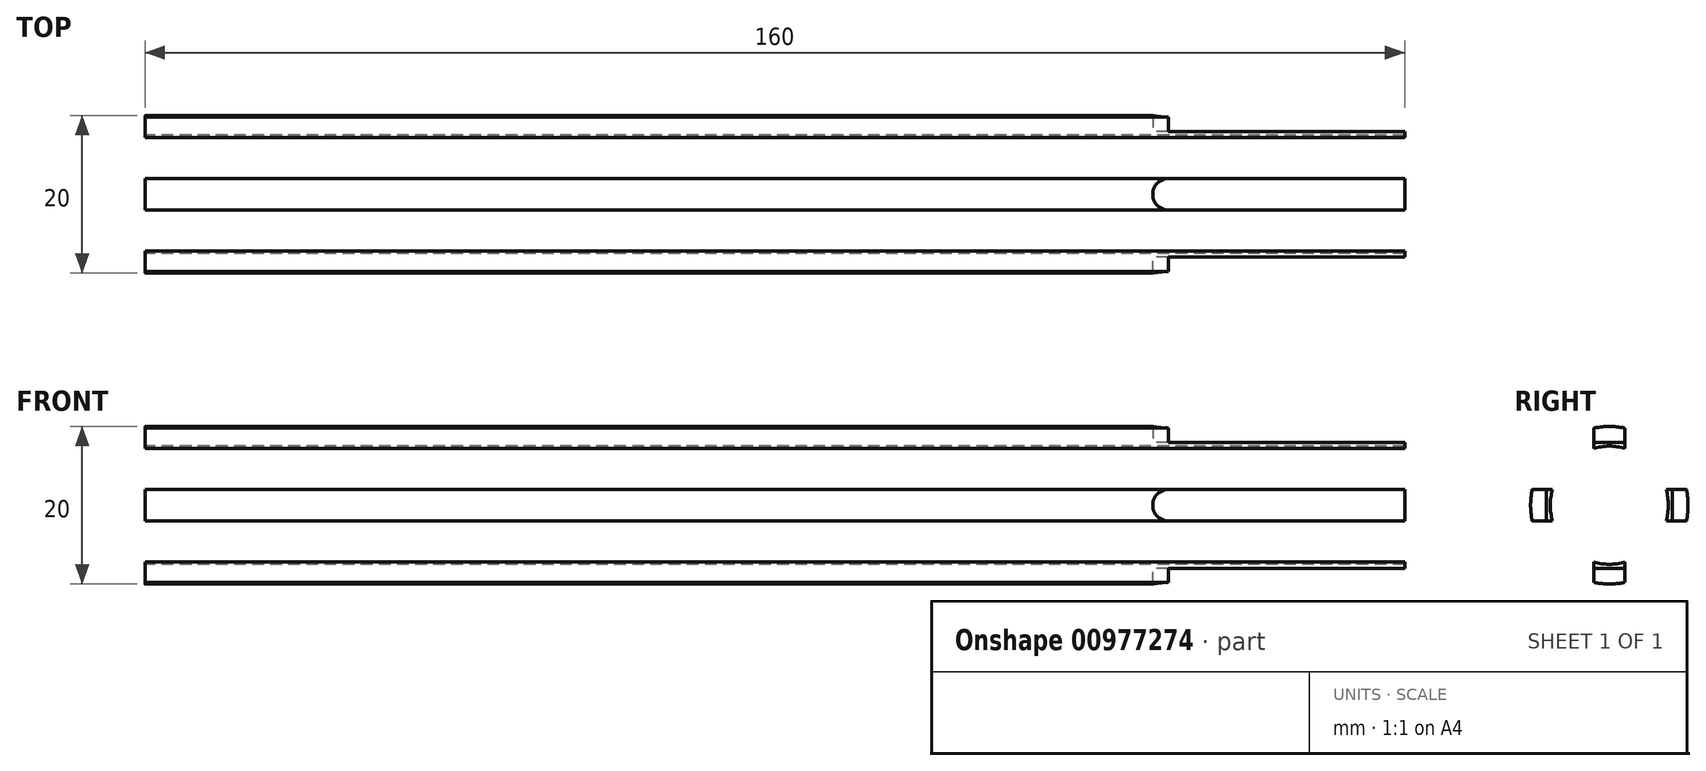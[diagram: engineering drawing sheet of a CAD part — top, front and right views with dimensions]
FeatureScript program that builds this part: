
annotation { "Feature Type Name" : "Feature", "Feature Type Description" : "" }
export const myFeature = defineFeature(function(context is Context, id is Id, definition is map)
    precondition{}
    {
        {
            var Q0;
            Q0=qCreatedBy(makeId("Right.planeOp"),FACE);
            var sketch = newSketch(context, id + "F0", { "sketchPlane" : qUnion([Q0])});
            skCircle(sketch, "E0", {"center": v(0, 0) * mm, "radius": 7.5 * mm});
            skCircle(sketch, "E1", {"center": v(0, 0) * mm, "radius": 10 * mm});
            skLineSegment(sketch, "E2.bottom", {"start": v(-2, 12.5) * mm, "end": v(2, 12.5) * mm});
            skLineSegment(sketch, "E2.top", {"start": v(-2, -12.5) * mm, "end": v(2, -12.5) * mm});
            skLineSegment(sketch, "E2.left", {"start": v(-2, 12.5) * mm, "end": v(-2, -12.5) * mm});
            skLineSegment(sketch, "E2.right", {"start": v(2, 12.5) * mm, "end": v(2, -12.5) * mm});
            skLineSegment(sketch, "E3.bottom", {"start": v(12.5, -2) * mm, "end": v(-12.5, -2) * mm});
            skLineSegment(sketch, "E3.top", {"start": v(12.5, 2) * mm, "end": v(-12.5, 2) * mm});
            skLineSegment(sketch, "E3.left", {"start": v(12.5, -2) * mm, "end": v(12.5, 2) * mm});
            skLineSegment(sketch, "E3.right", {"start": v(-12.5, -2) * mm, "end": v(-12.5, 2) * mm});
            skLineSegment(sketch, "E4.bottom", {"start": v(-2, 8) * mm, "end": v(2, 8) * mm});
            skLineSegment(sketch, "E4.top", {"start": v(-2, -8) * mm, "end": v(2, -8) * mm});
            skLineSegment(sketch, "E4.left", {"start": v(-2, 8) * mm, "end": v(-2, -8) * mm});
            skLineSegment(sketch, "E4.right", {"start": v(2, 8) * mm, "end": v(2, -8) * mm});
            skLineSegment(sketch, "E5.bottom", {"start": v(8, 2) * mm, "end": v(-8, 2) * mm});
            skLineSegment(sketch, "E5.top", {"start": v(8, -2) * mm, "end": v(-8, -2) * mm});
            skLineSegment(sketch, "E5.left", {"start": v(8, 2) * mm, "end": v(8, -2) * mm});
            skLineSegment(sketch, "E5.right", {"start": v(-8, 2) * mm, "end": v(-8, -2) * mm});
            skSolve(sketch);
        }
        {
            var Q0;
            {var subQ5=sQuery(id+"F0.wireOp",EDGE,"E4.right");var subQ9=sQuery(id+"F0.wireOp",EDGE,"E0");var subQ10=makeQuery(id+"F0.imprint","INTERSECT",VERTEX,{"disambiguationData":[OD(0.0)],"derivedFrom":[subQ9,subQ5]});Q0=makeQuery(id+"F0.imprint","IMPRINT",FACE,{"disambiguationData":[TD([[makeQuery(id+"F0.imprint","IMPRINT",EDGE,{"disambiguationData":[TD([[subQ10,1.0]])],"derivedFrom":subQ9}),-1.0]])]});}
            var Q1;
            {var subQ0=sQuery(id+"F0.wireOp",EDGE,"E4.left");var subQ8=sQuery(id+"F0.wireOp",EDGE,"E0");var subQ11=makeQuery(id+"F0.imprint","INTERSECT",VERTEX,{"disambiguationData":[OD(0.0)],"derivedFrom":[subQ8,subQ0]});Q1=makeQuery(id+"F0.imprint","IMPRINT",FACE,{"disambiguationData":[TD([[makeQuery(id+"F0.imprint","IMPRINT",EDGE,{"disambiguationData":[TD([[subQ11,-1.0]])],"derivedFrom":subQ8}),-1.0]])]});}
            var Q2;
            {var subQ0=sQuery(id+"F0.wireOp",EDGE,"E4.right");var subQ1=sQuery(id+"F0.wireOp",EDGE,"E0");var subQ2=makeQuery(id+"F0.imprint","INTERSECT",VERTEX,{"disambiguationData":[OD(0.0)],"derivedFrom":[subQ1,subQ0]});Q2=makeQuery(id+"F0.imprint","IMPRINT",FACE,{"disambiguationData":[TD([[makeQuery(id+"F0.imprint","IMPRINT",EDGE,{"disambiguationData":[TD([[subQ2,1.0]])],"derivedFrom":subQ1}),1.0]])]});}
            var Q3;
            {var subQ0=sQuery(id+"F0.wireOp",EDGE,"E4.right");var subQ1=sQuery(id+"F0.wireOp",EDGE,"E0");var subQ2=makeQuery(id+"F0.imprint","INTERSECT",VERTEX,{"disambiguationData":[OD(0.0)],"derivedFrom":[subQ1,subQ0]});Q3=makeQuery(id+"F0.imprint","IMPRINT",FACE,{"disambiguationData":[TD([[makeQuery(id+"F0.imprint","IMPRINT",EDGE,{"disambiguationData":[TD([[subQ2,-1.0]])],"derivedFrom":subQ1}),1.0]])]});}
            var Q4;
            {var subQ0=sQuery(id+"F0.wireOp",EDGE,"E4.left");var subQ1=sQuery(id+"F0.wireOp",EDGE,"E0");var subQ2=makeQuery(id+"F0.imprint","INTERSECT",VERTEX,{"disambiguationData":[OD(0.0)],"derivedFrom":[subQ1,subQ0]});Q4=makeQuery(id+"F0.imprint","IMPRINT",FACE,{"disambiguationData":[TD([[makeQuery(id+"F0.imprint","IMPRINT",EDGE,{"disambiguationData":[TD([[subQ2,-1.0]])],"derivedFrom":subQ1}),1.0]])]});}
            var Q5;
            {var subQ0=sQuery(id+"F0.wireOp",EDGE,"E5.bottom");var subQ1=sQuery(id+"F0.wireOp",EDGE,"E0");var subQ2=makeQuery(id+"F0.imprint","INTERSECT",VERTEX,{"disambiguationData":[OD(1.0)],"derivedFrom":[subQ1,subQ0]});Q5=makeQuery(id+"F0.imprint","IMPRINT",FACE,{"disambiguationData":[TD([[makeQuery(id+"F0.imprint","IMPRINT",EDGE,{"disambiguationData":[TD([[subQ2,-1.0]])],"derivedFrom":subQ1}),1.0]])]});}
            var Q6;
            {var subQ0=sQuery(id+"F0.wireOp",EDGE,"E5.bottom");var subQ1=sQuery(id+"F0.wireOp",EDGE,"E0");var subQ2=makeQuery(id+"F0.imprint","INTERSECT",VERTEX,{"disambiguationData":[OD(0.0)],"derivedFrom":[subQ1,subQ0]});Q6=makeQuery(id+"F0.imprint","IMPRINT",FACE,{"disambiguationData":[TD([[makeQuery(id+"F0.imprint","IMPRINT",EDGE,{"disambiguationData":[TD([[subQ2,1.0]])],"derivedFrom":subQ1}),1.0]])]});}
            var Q7;
            {var subQ0=sQuery(id+"F0.wireOp",EDGE,"E5.bottom");var subQ1=sQuery(id+"F0.wireOp",EDGE,"E4.left");var subQ2=makeQuery(id+"F0.imprint","INTERSECT",VERTEX,{"derivedFrom":[subQ1,subQ0]});Q7=makeQuery(id+"F0.imprint","IMPRINT",FACE,{"disambiguationData":[TD([[makeQuery(id+"F0.imprint","IMPRINT",EDGE,{"disambiguationData":[TD([[subQ2,-1.0]])],"derivedFrom":subQ1}),1.0]])]});}
            var Q8;
            {var subQ0=sQuery(id+"F0.wireOp",EDGE,"E4.left");var subQ1=sQuery(id+"F0.wireOp",EDGE,"E0");var subQ2=makeQuery(id+"F0.imprint","INTERSECT",VERTEX,{"disambiguationData":[OD(1.0)],"derivedFrom":[subQ1,subQ0]});Q8=makeQuery(id+"F0.imprint","IMPRINT",FACE,{"disambiguationData":[TD([[makeQuery(id+"F0.imprint","IMPRINT",EDGE,{"disambiguationData":[TD([[subQ2,-1.0]])],"derivedFrom":subQ1}),1.0]])]});}
            var Q9;
            {var subQ0=sQuery(id+"F0.wireOp",EDGE,"E5.top");var subQ1=sQuery(id+"F0.wireOp",EDGE,"E0");var subQ2=makeQuery(id+"F0.imprint","INTERSECT",VERTEX,{"disambiguationData":[OD(0.0)],"derivedFrom":[subQ1,subQ0]});Q9=makeQuery(id+"F0.imprint","IMPRINT",FACE,{"disambiguationData":[TD([[makeQuery(id+"F0.imprint","IMPRINT",EDGE,{"disambiguationData":[TD([[subQ2,-1.0]])],"derivedFrom":subQ1}),1.0]])]});}
            var Q10;
            {var subQ0=sQuery(id+"F0.wireOp",EDGE,"E4.right");var subQ1=sQuery(id+"F0.wireOp",EDGE,"E0");var subQ2=makeQuery(id+"F0.imprint","INTERSECT",VERTEX,{"disambiguationData":[OD(1.0)],"derivedFrom":[subQ1,subQ0]});Q10=makeQuery(id+"F0.imprint","IMPRINT",FACE,{"disambiguationData":[TD([[makeQuery(id+"F0.imprint","IMPRINT",EDGE,{"disambiguationData":[TD([[subQ2,-1.0]])],"derivedFrom":subQ1}),1.0]])]});}
            var Q11;
            {var subQ5=sQuery(id+"F0.wireOp",EDGE,"E4.right");var subQ9=sQuery(id+"F0.wireOp",EDGE,"E0");var subQ10=makeQuery(id+"F0.imprint","INTERSECT",VERTEX,{"disambiguationData":[OD(1.0)],"derivedFrom":[subQ9,subQ5]});Q11=makeQuery(id+"F0.imprint","IMPRINT",FACE,{"disambiguationData":[TD([[makeQuery(id+"F0.imprint","IMPRINT",EDGE,{"disambiguationData":[TD([[subQ10,-1.0]])],"derivedFrom":subQ9}),-1.0]])]});}
            var Q12;
            {var subQ0=sQuery(id+"F0.wireOp",EDGE,"E5.top");var subQ9=sQuery(id+"F0.wireOp",EDGE,"E0");var subQ11=makeQuery(id+"F0.imprint","INTERSECT",VERTEX,{"disambiguationData":[OD(0.0)],"derivedFrom":[subQ9,subQ0]});Q12=makeQuery(id+"F0.imprint","IMPRINT",FACE,{"disambiguationData":[TD([[makeQuery(id+"F0.imprint","IMPRINT",EDGE,{"disambiguationData":[TD([[subQ11,-1.0]])],"derivedFrom":subQ9}),-1.0]])]});}
            var Q13;
            {var subQ5=sQuery(id+"F0.wireOp",EDGE,"E4.top");Q13=makeQuery(id+"F0.imprint","IMPRINT",FACE,{"disambiguationData":[TD([[makeQuery(id+"F0.imprint","IMPRINT",EDGE,{"derivedFrom":subQ5}),1.0]])]});}
            var Q14;
            {var subQ5=sQuery(id+"F0.wireOp",EDGE,"E5.left");Q14=makeQuery(id+"F0.imprint","IMPRINT",FACE,{"disambiguationData":[TD([[makeQuery(id+"F0.imprint","IMPRINT",EDGE,{"derivedFrom":subQ5}),-1.0]])]});}
            var Q15;
            {var subQ5=sQuery(id+"F0.wireOp",EDGE,"E4.bottom");Q15=makeQuery(id+"F0.imprint","IMPRINT",FACE,{"disambiguationData":[TD([[makeQuery(id+"F0.imprint","IMPRINT",EDGE,{"derivedFrom":subQ5}),-1.0]])]});}
            var Q16;
            {var subQ5=sQuery(id+"F0.wireOp",EDGE,"E5.right");Q16=makeQuery(id+"F0.imprint","IMPRINT",FACE,{"disambiguationData":[TD([[makeQuery(id+"F0.imprint","IMPRINT",EDGE,{"derivedFrom":subQ5}),1.0]])]});}
            extrude(context, id + "F1", {"entities" : qUnion([Q0, Q1, Q2, Q3, Q4, Q5, Q6, Q7, Q8, Q9, Q10, Q11, Q12, Q13, Q14, Q15, Q16]), "depth" : 30 * mm, "offsetDistance" : 25 * mm});
        }
        {
            var Q0;
            {var subQ5=sQuery(id+"F0.wireOp",EDGE,"E4.bottom");Q0=makeQuery(id+"F0.imprint","IMPRINT",FACE,{"disambiguationData":[TD([[makeQuery(id+"F0.imprint","IMPRINT",EDGE,{"derivedFrom":subQ5}),1.0]])]});}
            var Q1;
            {var subQ5=sQuery(id+"F0.wireOp",EDGE,"E4.right");var subQ9=sQuery(id+"F0.wireOp",EDGE,"E0");var subQ10=makeQuery(id+"F0.imprint","INTERSECT",VERTEX,{"disambiguationData":[OD(0.0)],"derivedFrom":[subQ9,subQ5]});Q1=makeQuery(id+"F0.imprint","IMPRINT",FACE,{"disambiguationData":[TD([[makeQuery(id+"F0.imprint","IMPRINT",EDGE,{"disambiguationData":[TD([[subQ10,1.0]])],"derivedFrom":subQ9}),-1.0]])]});}
            var Q2;
            {var subQ5=sQuery(id+"F0.wireOp",EDGE,"E4.bottom");Q2=makeQuery(id+"F0.imprint","IMPRINT",FACE,{"disambiguationData":[TD([[makeQuery(id+"F0.imprint","IMPRINT",EDGE,{"derivedFrom":subQ5}),-1.0]])]});}
            var Q3;
            {var subQ0=sQuery(id+"F0.wireOp",EDGE,"E4.left");var subQ8=sQuery(id+"F0.wireOp",EDGE,"E0");var subQ11=makeQuery(id+"F0.imprint","INTERSECT",VERTEX,{"disambiguationData":[OD(0.0)],"derivedFrom":[subQ8,subQ0]});Q3=makeQuery(id+"F0.imprint","IMPRINT",FACE,{"disambiguationData":[TD([[makeQuery(id+"F0.imprint","IMPRINT",EDGE,{"disambiguationData":[TD([[subQ11,-1.0]])],"derivedFrom":subQ8}),-1.0]])]});}
            var Q4;
            {var subQ5=sQuery(id+"F0.wireOp",EDGE,"E5.right");Q4=makeQuery(id+"F0.imprint","IMPRINT",FACE,{"disambiguationData":[TD([[makeQuery(id+"F0.imprint","IMPRINT",EDGE,{"derivedFrom":subQ5}),1.0]])]});}
            var Q5;
            {var subQ5=sQuery(id+"F0.wireOp",EDGE,"E5.right");Q5=makeQuery(id+"F0.imprint","IMPRINT",FACE,{"disambiguationData":[TD([[makeQuery(id+"F0.imprint","IMPRINT",EDGE,{"derivedFrom":subQ5}),-1.0]])]});}
            var Q6;
            {var subQ0=sQuery(id+"F0.wireOp",EDGE,"E4.left");var subQ1=sQuery(id+"F0.wireOp",EDGE,"E0");var subQ2=makeQuery(id+"F0.imprint","INTERSECT",VERTEX,{"disambiguationData":[OD(0.0)],"derivedFrom":[subQ1,subQ0]});Q6=makeQuery(id+"F0.imprint","IMPRINT",FACE,{"disambiguationData":[TD([[makeQuery(id+"F0.imprint","IMPRINT",EDGE,{"disambiguationData":[TD([[subQ2,-1.0]])],"derivedFrom":subQ1}),1.0]])]});}
            var Q7;
            {var subQ0=sQuery(id+"F0.wireOp",EDGE,"E4.right");var subQ1=sQuery(id+"F0.wireOp",EDGE,"E0");var subQ2=makeQuery(id+"F0.imprint","INTERSECT",VERTEX,{"disambiguationData":[OD(0.0)],"derivedFrom":[subQ1,subQ0]});Q7=makeQuery(id+"F0.imprint","IMPRINT",FACE,{"disambiguationData":[TD([[makeQuery(id+"F0.imprint","IMPRINT",EDGE,{"disambiguationData":[TD([[subQ2,-1.0]])],"derivedFrom":subQ1}),1.0]])]});}
            var Q8;
            {var subQ0=sQuery(id+"F0.wireOp",EDGE,"E4.right");var subQ1=sQuery(id+"F0.wireOp",EDGE,"E0");var subQ2=makeQuery(id+"F0.imprint","INTERSECT",VERTEX,{"disambiguationData":[OD(0.0)],"derivedFrom":[subQ1,subQ0]});Q8=makeQuery(id+"F0.imprint","IMPRINT",FACE,{"disambiguationData":[TD([[makeQuery(id+"F0.imprint","IMPRINT",EDGE,{"disambiguationData":[TD([[subQ2,1.0]])],"derivedFrom":subQ1}),1.0]])]});}
            var Q9;
            {var subQ5=sQuery(id+"F0.wireOp",EDGE,"E5.left");Q9=makeQuery(id+"F0.imprint","IMPRINT",FACE,{"disambiguationData":[TD([[makeQuery(id+"F0.imprint","IMPRINT",EDGE,{"derivedFrom":subQ5}),1.0]])]});}
            var Q10;
            {var subQ5=sQuery(id+"F0.wireOp",EDGE,"E5.left");Q10=makeQuery(id+"F0.imprint","IMPRINT",FACE,{"disambiguationData":[TD([[makeQuery(id+"F0.imprint","IMPRINT",EDGE,{"derivedFrom":subQ5}),-1.0]])]});}
            var Q11;
            {var subQ0=sQuery(id+"F0.wireOp",EDGE,"E5.bottom");var subQ1=sQuery(id+"F0.wireOp",EDGE,"E0");var subQ2=makeQuery(id+"F0.imprint","INTERSECT",VERTEX,{"disambiguationData":[OD(0.0)],"derivedFrom":[subQ1,subQ0]});Q11=makeQuery(id+"F0.imprint","IMPRINT",FACE,{"disambiguationData":[TD([[makeQuery(id+"F0.imprint","IMPRINT",EDGE,{"disambiguationData":[TD([[subQ2,1.0]])],"derivedFrom":subQ1}),1.0]])]});}
            var Q12;
            {var subQ0=sQuery(id+"F0.wireOp",EDGE,"E5.bottom");var subQ1=sQuery(id+"F0.wireOp",EDGE,"E4.left");var subQ2=makeQuery(id+"F0.imprint","INTERSECT",VERTEX,{"derivedFrom":[subQ1,subQ0]});Q12=makeQuery(id+"F0.imprint","IMPRINT",FACE,{"disambiguationData":[TD([[makeQuery(id+"F0.imprint","IMPRINT",EDGE,{"disambiguationData":[TD([[subQ2,-1.0]])],"derivedFrom":subQ1}),1.0]])]});}
            var Q13;
            {var subQ0=sQuery(id+"F0.wireOp",EDGE,"E5.bottom");var subQ1=sQuery(id+"F0.wireOp",EDGE,"E0");var subQ2=makeQuery(id+"F0.imprint","INTERSECT",VERTEX,{"disambiguationData":[OD(1.0)],"derivedFrom":[subQ1,subQ0]});Q13=makeQuery(id+"F0.imprint","IMPRINT",FACE,{"disambiguationData":[TD([[makeQuery(id+"F0.imprint","IMPRINT",EDGE,{"disambiguationData":[TD([[subQ2,-1.0]])],"derivedFrom":subQ1}),1.0]])]});}
            var Q14;
            {var subQ0=sQuery(id+"F0.wireOp",EDGE,"E5.top");var subQ1=sQuery(id+"F0.wireOp",EDGE,"E0");var subQ2=makeQuery(id+"F0.imprint","INTERSECT",VERTEX,{"disambiguationData":[OD(0.0)],"derivedFrom":[subQ1,subQ0]});Q14=makeQuery(id+"F0.imprint","IMPRINT",FACE,{"disambiguationData":[TD([[makeQuery(id+"F0.imprint","IMPRINT",EDGE,{"disambiguationData":[TD([[subQ2,-1.0]])],"derivedFrom":subQ1}),1.0]])]});}
            var Q15;
            {var subQ0=sQuery(id+"F0.wireOp",EDGE,"E5.top");var subQ9=sQuery(id+"F0.wireOp",EDGE,"E0");var subQ11=makeQuery(id+"F0.imprint","INTERSECT",VERTEX,{"disambiguationData":[OD(0.0)],"derivedFrom":[subQ9,subQ0]});Q15=makeQuery(id+"F0.imprint","IMPRINT",FACE,{"disambiguationData":[TD([[makeQuery(id+"F0.imprint","IMPRINT",EDGE,{"disambiguationData":[TD([[subQ11,-1.0]])],"derivedFrom":subQ9}),-1.0]])]});}
            var Q16;
            {var subQ5=sQuery(id+"F0.wireOp",EDGE,"E4.top");Q16=makeQuery(id+"F0.imprint","IMPRINT",FACE,{"disambiguationData":[TD([[makeQuery(id+"F0.imprint","IMPRINT",EDGE,{"derivedFrom":subQ5}),1.0]])]});}
            var Q17;
            {var subQ5=sQuery(id+"F0.wireOp",EDGE,"E4.top");Q17=makeQuery(id+"F0.imprint","IMPRINT",FACE,{"disambiguationData":[TD([[makeQuery(id+"F0.imprint","IMPRINT",EDGE,{"derivedFrom":subQ5}),-1.0]])]});}
            var Q18;
            {var subQ0=sQuery(id+"F0.wireOp",EDGE,"E4.right");var subQ1=sQuery(id+"F0.wireOp",EDGE,"E0");var subQ2=makeQuery(id+"F0.imprint","INTERSECT",VERTEX,{"disambiguationData":[OD(1.0)],"derivedFrom":[subQ1,subQ0]});Q18=makeQuery(id+"F0.imprint","IMPRINT",FACE,{"disambiguationData":[TD([[makeQuery(id+"F0.imprint","IMPRINT",EDGE,{"disambiguationData":[TD([[subQ2,-1.0]])],"derivedFrom":subQ1}),1.0]])]});}
            var Q19;
            {var subQ5=sQuery(id+"F0.wireOp",EDGE,"E4.right");var subQ9=sQuery(id+"F0.wireOp",EDGE,"E0");var subQ10=makeQuery(id+"F0.imprint","INTERSECT",VERTEX,{"disambiguationData":[OD(1.0)],"derivedFrom":[subQ9,subQ5]});Q19=makeQuery(id+"F0.imprint","IMPRINT",FACE,{"disambiguationData":[TD([[makeQuery(id+"F0.imprint","IMPRINT",EDGE,{"disambiguationData":[TD([[subQ10,-1.0]])],"derivedFrom":subQ9}),-1.0]])]});}
            var Q20;
            {var subQ0=sQuery(id+"F0.wireOp",EDGE,"E4.left");var subQ1=sQuery(id+"F0.wireOp",EDGE,"E0");var subQ2=makeQuery(id+"F0.imprint","INTERSECT",VERTEX,{"disambiguationData":[OD(1.0)],"derivedFrom":[subQ1,subQ0]});Q20=makeQuery(id+"F0.imprint","IMPRINT",FACE,{"disambiguationData":[TD([[makeQuery(id+"F0.imprint","IMPRINT",EDGE,{"disambiguationData":[TD([[subQ2,-1.0]])],"derivedFrom":subQ1}),1.0]])]});}
            extrude(context, id + "F2", {"entities" : qUnion([Q0, Q1, Q2, Q3, Q4, Q5, Q6, Q7, Q8, Q9, Q10, Q11, Q12, Q13, Q14, Q15, Q16, Q17, Q18, Q19, Q20]), "operationType" : NewBodyOperationType.ADD, "oppositeDirection" : true, "depth" : 130 * mm, "offsetDistance" : 25 * mm});
        }
        {
            var Q0;
            Q0=makeQuery(id+"F1.opExtrude","SWEPT_FACE",FACE,{"disambiguationData":[OSD([sQuery(id+"F0.wireOp",EDGE,"E4.bottom")])]});
            var sketch = newSketch(context, id + "F3", { "sketchPlane" : qUnion([Q0])});
            skCircle(sketch, "E6", {"center": v(0, 0) * mm, "radius": 2 * mm});
            skSolve(sketch);
        }
        {
            var Q0;
            Q0=qSketchRegion(id+"F3",true);
            extrude(context, id + "F4", {"entities" : qUnion([Q0]), "operationType" : NewBodyOperationType.REMOVE, "depth" : 25 * mm, "offsetDistance" : 25 * mm});
        }
        {
            var Q0;
            Q0=makeQuery(id+"F1.opExtrude","SWEPT_FACE",FACE,{"disambiguationData":[OSD([sQuery(id+"F0.wireOp",EDGE,"E5.right")])]});
            var sketch = newSketch(context, id + "F5", { "sketchPlane" : qUnion([Q0])});
            skCircle(sketch, "E7", {"center": v(0, 0) * mm, "radius": 2 * mm});
            skSolve(sketch);
        }
        {
            var Q0;
            Q0=qSketchRegion(id+"F5",true);
            extrude(context, id + "F6", {"entities" : qUnion([Q0]), "operationType" : NewBodyOperationType.REMOVE, "depth" : 25 * mm, "offsetDistance" : 25 * mm});
        }
        {
            var Q0;
            Q0=makeQuery(id+"F1.opExtrude","SWEPT_FACE",FACE,{"disambiguationData":[OSD([sQuery(id+"F0.wireOp",EDGE,"E4.top")])]});
            var sketch = newSketch(context, id + "F7", { "sketchPlane" : qUnion([Q0])});
            skCircle(sketch, "E8", {"center": v(0, 0) * mm, "radius": 2 * mm});
            skSolve(sketch);
        }
        {
            var Q0;
            Q0=qSketchRegion(id+"F7",true);
            extrude(context, id + "F8", {"entities" : qUnion([Q0]), "operationType" : NewBodyOperationType.REMOVE, "depth" : 25 * mm, "offsetDistance" : 25 * mm});
        }
        {
            var Q0;
            Q0=makeQuery(id+"F1.opExtrude","SWEPT_FACE",FACE,{"disambiguationData":[OSD([sQuery(id+"F0.wireOp",EDGE,"E5.left")])]});
            var sketch = newSketch(context, id + "F9", { "sketchPlane" : qUnion([Q0])});
            skCircle(sketch, "E9", {"center": v(0, 0) * mm, "radius": 2 * mm});
            skSolve(sketch);
        }
        {
            var Q0;
            Q0=qSketchRegion(id+"F9",true);
            extrude(context, id + "F10", {"entities" : qUnion([Q0]), "operationType" : NewBodyOperationType.REMOVE, "depth" : 25 * mm, "offsetDistance" : 25 * mm});
        }
        {
            var Q0;
            Q0=makeQuery(id+"F1.opExtrude","CAP_FACE",FACE,{"disambiguationData":[OSD([sQuery(id+"F0.wireOp",EDGE,"E1"),sQuery(id+"F0.wireOp",EDGE,"E2.left"),sQuery(id+"F0.wireOp",EDGE,"E2.right"),sQuery(id+"F0.wireOp",EDGE,"E3.bottom"),sQuery(id+"F0.wireOp",EDGE,"E3.top"),sQuery(id+"F0.wireOp",EDGE,"E4.bottom"),sQuery(id+"F0.wireOp",EDGE,"E4.top"),sQuery(id+"F0.wireOp",EDGE,"E5.left"),sQuery(id+"F0.wireOp",EDGE,"E5.right")])],"isStart":false});
            var sketch = newSketch(context, id + "F11", { "sketchPlane" : qUnion([Q0])});
            skPoint(sketch, "E10", {"position": v(0, 0) * mm});
            skSolve(sketch);
        }
        {
            var Q0;
            Q0=sQuery(id+"F11.wireOp",VERTEX,"E10");
            var Q1;
            Q1=makeQuery(id+"F1.opExtrude","SWEPT_BODY",BODY,{"disambiguationData":[OSD([sQuery(id+"F0.wireOp",EDGE,"E1"),sQuery(id+"F0.wireOp",EDGE,"E2.left"),sQuery(id+"F0.wireOp",EDGE,"E2.right"),sQuery(id+"F0.wireOp",EDGE,"E3.bottom"),sQuery(id+"F0.wireOp",EDGE,"E3.top"),sQuery(id+"F0.wireOp",EDGE,"E4.bottom"),sQuery(id+"F0.wireOp",EDGE,"E4.top"),sQuery(id+"F0.wireOp",EDGE,"E5.left"),sQuery(id+"F0.wireOp",EDGE,"E5.right")])]});
            hole(context, id + "F12", {"style" : HoleStyle.SIMPLE, "endStyle" : HoleEndStyle.BLIND, "holeDiameter" : 5 * mm, "majorDiameter" : 5 * mm, "holeDepth" : 20 * mm, "isTappedThrough" : true, "tappedDepth" : 12 * mm, "tapClearance" : 3, "locations" : qUnion([Q0]), "scope" : qUnion([Q1])});
        }
    });
